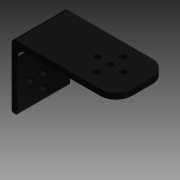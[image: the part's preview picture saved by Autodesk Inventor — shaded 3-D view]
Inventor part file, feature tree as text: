
AUTODESK INVENTOR PART (.ipt)
format: ipt  version: 2014 SP2 (Build 180246200, 246)  size: 212,992 bytes
history: native  units: in
note: dims shown in document units (in); Inventor stores cm internally (conversion verified against a paired STEP export)
features: sketch x7, extrude x6, mirror x4, fillet x4, pattern_circular x2, projected_geometry x2
ambient origin geometry x8: Origin, YZ Plane, XZ Plane, XY Plane, X Axis, Y Axis, Z Axis, Center Point
bodies: Solid1 (feature_tree)
feature tree (25):
  extrude  "Extrusion1"  Depth=0.1181in
  mirror  "Mirror1"
  mirror  "Mirror2"
  extrude  "Extrusion4"  Depth=2.0472in
  mirror  "Mirror3"
  extrude  "Extrusion11"  Depth=0.3937in TaperAngle=0.0deg
  extrude  "Extrusion13"  Depth=0.0787in
  mirror  "Mirror4"
  extrude  "Extrusion14"  Depth=0.3937in
  pattern_circular  "Circular Pattern6"  Count=2  [1 undecoded]
  extrude  "Extrusion15"  Depth=0.1181in
  pattern_circular  "Circular Pattern7"  Count=4 Angle=360.0deg
  fillet  "Fillet1"  Radius=0.5118in
  sketch  "Sketch18"  dims[d73=0.3937in d74=0.0in d75=1.5748in d76=360.0deg d78=0.5118in d79=0.6299in d80=0.1181in d81=0.1181in d82=0.3937in d83=0.0in d84=1.5748in d85=360.0deg d87=0.315in d93=1.0236in d94=0.1575in d95=0.0787in d96=0.0394in]
  fillet  "Fillet2"  Radius=0.6299in
  fillet  "Fillet3"  Radius=0.1181in
  fillet  "Fillet4"  Radius=0.1181in
  sketch  "Sketch1"  dims[d0=0.7087in d1=0.1181in]
  sketch  "Sketch4"  dims[d2=0.1181in d3=2.0472in]
  projected_geometry  "Projected Loop1"
  sketch  "Sketch11"  dims[d4=0.3937in d5=0.0in d16=0.1969in d17=0.0in]
  projected_geometry  "Projected Loop3"
  sketch  "Sketch13"  dims[d54=0.3937in d55=0.0in d65=0.0787in]
  sketch  "Sketch14"  dims[d66=0.3937in d67=0.0in d68=0.5118in d69=0.7874in]
  sketch  "Sketch15"  dims[d71=0.1181in d72=0.1181in]
note: 1 required parameter value undecoded (feature->parameter linkage not recoverable at this tier; creation-order binding heuristic only, values carry confidence <= 0.55)
